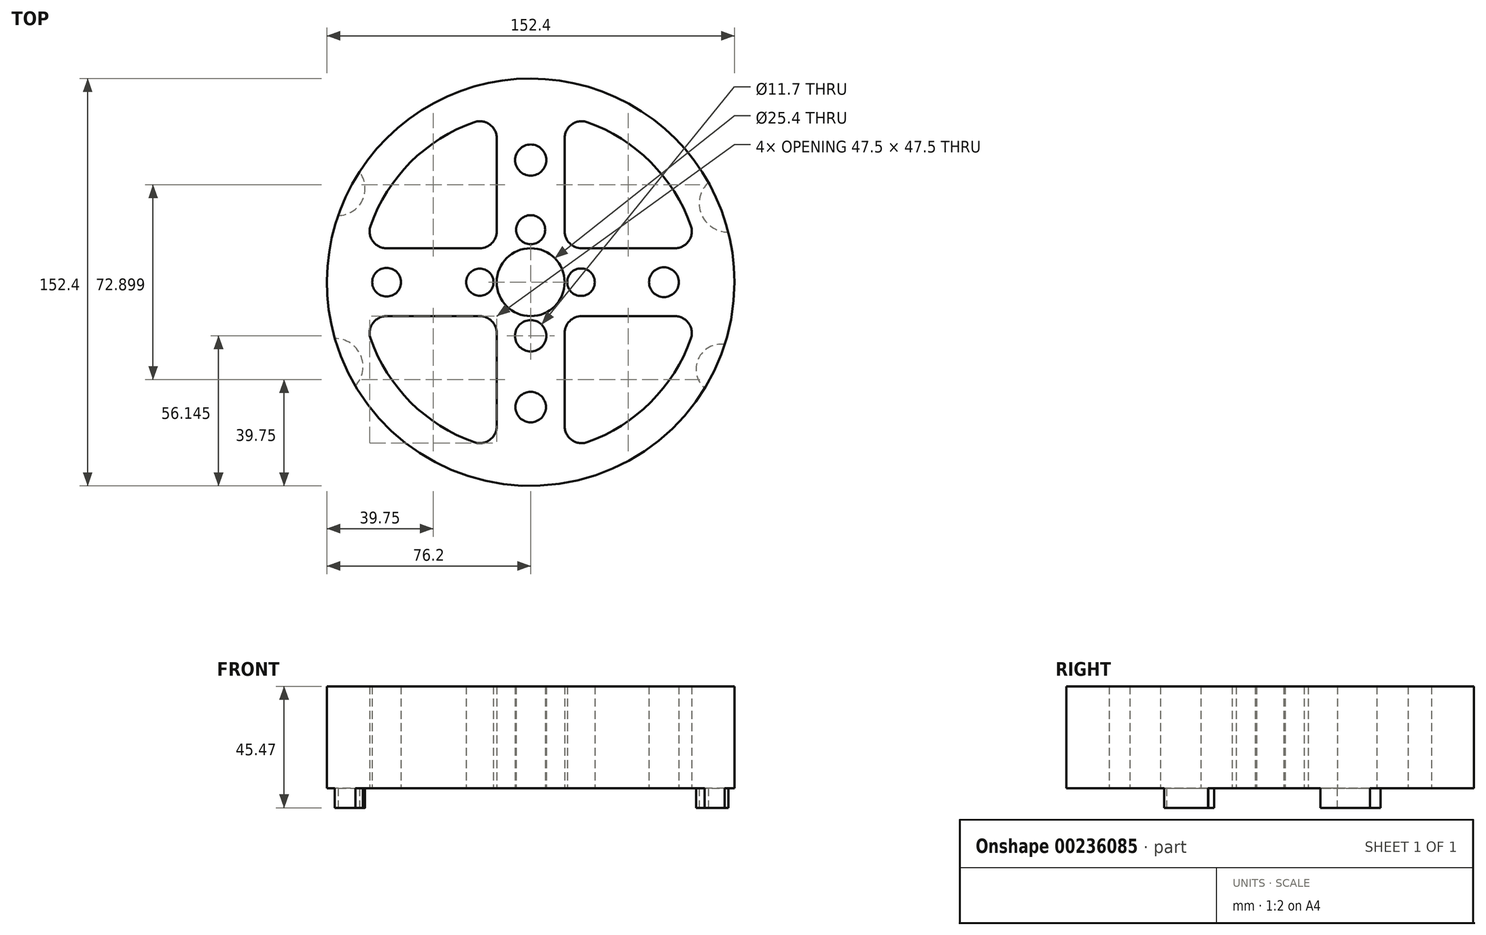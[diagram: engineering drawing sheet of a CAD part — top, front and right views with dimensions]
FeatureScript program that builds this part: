
annotation { "Feature Type Name" : "Feature", "Feature Type Description" : "" }
export const myFeature = defineFeature(function(context is Context, id is Id, definition is map)
    precondition{}
    {
        {
            var Q0;
            Q0=qCreatedBy(makeId("Top.planeOp"),FACE);
            var sketch = newSketch(context, id + "F0", { "sketchPlane" : qUnion([Q0])});
            skCircle(sketch, "E0", {"center": v(0, 0) * mm, "radius": 76.2 * mm});
            skArc(sketch, "E1", {"start": v(-21.17, 59.87) * mm, "mid": v(-44.9, 44.9) * mm, "end": v(-59.87, 21.17) * mm});
            skCircle(sketch, "E2", {"center": v(0, 0) * mm, "radius": 12.7 * mm});
            skLineSegment(sketch, "E3", {"start": v(0, 0) * mm, "end": v(0, 76.2) * mm});
            skLineSegment(sketch, "E4.0", {"start": v(12.7, 19.05) * mm, "end": v(12.7, 53.88) * mm});
            skLineSegment(sketch, "E5.0", {"start": v(-12.7, 19.05) * mm, "end": v(-12.7, 53.88) * mm});
            skLineSegment(sketch, "E6", {"start": v(0, 0) * mm, "end": v(0, -76.2) * mm});
            skLineSegment(sketch, "E7", {"start": v(0, 0) * mm, "end": v(76.2, 0) * mm});
            skLineSegment(sketch, "E8", {"start": v(0, 0) * mm, "end": v(-76.2, 0) * mm});
            skLineSegment(sketch, "E9.0", {"start": v(19.05, -12.7) * mm, "end": v(53.88, -12.7) * mm});
            skLineSegment(sketch, "E10.0", {"start": v(19.05, 12.7) * mm, "end": v(53.88, 12.7) * mm});
            skLineSegment(sketch, "E11.0", {"start": v(-12.7, -19.05) * mm, "end": v(-12.7, -53.88) * mm});
            skLineSegment(sketch, "E12.0", {"start": v(12.7, -19.05) * mm, "end": v(12.7, -53.88) * mm});
            skLineSegment(sketch, "E13.0", {"start": v(-19.05, 12.7) * mm, "end": v(-53.88, 12.7) * mm});
            skLineSegment(sketch, "E14.0", {"start": v(-19.05, -12.7) * mm, "end": v(-53.88, -12.7) * mm});
            skArc(sketch, "E15.trimOffspring", {"start": v(59.87, 21.17) * mm, "mid": v(44.9, 44.9) * mm, "end": v(21.17, 59.87) * mm});
            skLineSegment(sketch, "E16.trimOffspring", {"start": v(75.13, -12.7) * mm, "end": v(76.2, -12.7) * mm});
            skLineSegment(sketch, "E17.trimOffspring", {"start": v(75.13, 12.7) * mm, "end": v(76.2, 12.7) * mm});
            skArc(sketch, "E18.trimOffspring", {"start": v(-59.87, -21.17) * mm, "mid": v(-44.9, -44.9) * mm, "end": v(-21.17, -59.87) * mm});
            skArc(sketch, "E19.trimOffspring", {"start": v(21.17, -59.87) * mm, "mid": v(44.9, -44.9) * mm, "end": v(59.87, -21.17) * mm});
            skLineSegment(sketch, "E20.trimOffspring", {"start": v(-12.7, -75.13) * mm, "end": v(-12.7, -76.2) * mm});
            skLineSegment(sketch, "E21.trimOffspring", {"start": v(12.7, -75.13) * mm, "end": v(12.7, -76.2) * mm});
            skLineSegment(sketch, "E22.trimOffspring", {"start": v(-75.13, 12.7) * mm, "end": v(-76.2, 12.7) * mm});
            skLineSegment(sketch, "E23.trimOffspring", {"start": v(-12.7, 75.13) * mm, "end": v(-12.7, 76.2) * mm});
            skLineSegment(sketch, "E24.trimOffspring", {"start": v(12.7, 75.13) * mm, "end": v(12.7, 76.2) * mm});
            skPoint(sketch, "E25.visualSharp", {"position": v(12.7, 62.22) * mm});
            skArc(sketch, "E25.filletArc", {"start": v(21.17, 59.87) * mm, "mid": v(15.38, 59.07) * mm, "end": v(12.7, 53.88) * mm});
            skPoint(sketch, "E26.visualSharp", {"position": v(12.7, 12.7) * mm});
            skArc(sketch, "E26.filletArc", {"start": v(12.7, 19.05) * mm, "mid": v(14.56, 14.56) * mm, "end": v(19.05, 12.7) * mm});
            skPoint(sketch, "E27.visualSharp", {"position": v(62.22, 12.7) * mm});
            skArc(sketch, "E27.filletArc", {"start": v(53.88, 12.7) * mm, "mid": v(59.07, 15.38) * mm, "end": v(59.87, 21.17) * mm});
            skPoint(sketch, "E28.visualSharp", {"position": v(-12.7, 62.22) * mm});
            skArc(sketch, "E28.filletArc", {"start": v(-12.7, 53.88) * mm, "mid": v(-15.38, 59.07) * mm, "end": v(-21.17, 59.87) * mm});
            skPoint(sketch, "E29.visualSharp", {"position": v(-12.7, 12.7) * mm});
            skArc(sketch, "E29.filletArc", {"start": v(-19.05, 12.7) * mm, "mid": v(-14.56, 14.56) * mm, "end": v(-12.7, 19.05) * mm});
            skPoint(sketch, "E30.visualSharp", {"position": v(-62.22, 12.7) * mm});
            skArc(sketch, "E30.filletArc", {"start": v(-59.87, 21.17) * mm, "mid": v(-59.07, 15.38) * mm, "end": v(-53.88, 12.7) * mm});
            skPoint(sketch, "E31.visualSharp", {"position": v(-12.7, -12.7) * mm});
            skArc(sketch, "E31.filletArc", {"start": v(-12.7, -19.05) * mm, "mid": v(-14.56, -14.56) * mm, "end": v(-19.05, -12.7) * mm});
            skPoint(sketch, "E32.visualSharp", {"position": v(-12.7, -62.22) * mm});
            skArc(sketch, "E32.filletArc", {"start": v(-21.17, -59.87) * mm, "mid": v(-15.38, -59.07) * mm, "end": v(-12.7, -53.88) * mm});
            skPoint(sketch, "E33.visualSharp", {"position": v(-62.22, -12.7) * mm});
            skArc(sketch, "E33.filletArc", {"start": v(-53.88, -12.7) * mm, "mid": v(-59.07, -15.38) * mm, "end": v(-59.87, -21.17) * mm});
            skPoint(sketch, "E34.visualSharp", {"position": v(12.7, -12.7) * mm});
            skArc(sketch, "E34.filletArc", {"start": v(19.05, -12.7) * mm, "mid": v(14.56, -14.56) * mm, "end": v(12.7, -19.05) * mm});
            skPoint(sketch, "E35.visualSharp", {"position": v(12.7, -62.22) * mm});
            skArc(sketch, "E35.filletArc", {"start": v(12.7, -53.88) * mm, "mid": v(15.38, -59.07) * mm, "end": v(21.17, -59.87) * mm});
            skPoint(sketch, "E36.visualSharp", {"position": v(62.22, -12.7) * mm});
            skArc(sketch, "E36.filletArc", {"start": v(59.87, -21.17) * mm, "mid": v(59.07, -15.38) * mm, "end": v(53.88, -12.7) * mm});
            skArc(sketch, "E37", {"start": v(-72, 24.96) * mm, "mid": v(-62.94, 30.64) * mm, "end": v(-64.06, 41.27) * mm});
            skArc(sketch, "E38", {"start": v(-65.57, -38.83) * mm, "mid": v(-63.56, -27.41) * mm, "end": v(-73.24, -21.04) * mm});
            skArc(sketch, "E39", {"start": v(72.55, -23.3) * mm, "mid": v(62.67, -28.7) * mm, "end": v(65.03, -39.72) * mm});
            skArc(sketch, "E40", {"start": v(66.43, 37.33) * mm, "mid": v(63.8, 25.5) * mm, "end": v(73.86, 18.73) * mm});
            skLineSegment(sketch, "E41", {"start": v(-53.88, 0) * mm, "end": v(-19.02, 0) * mm});
            skCircle(sketch, "E42", {"center": v(-53.88, 0) * mm, "radius": 5.38 * mm});
            skCircle(sketch, "E43", {"center": v(-19.02, 0) * mm, "radius": 5.1 * mm});
            skCircle(sketch, "E44", {"center": v(18.81, 0) * mm, "radius": 5.14 * mm});
            skCircle(sketch, "E45", {"center": v(49.83, 0) * mm, "radius": 5.56 * mm});
            skCircle(sketch, "E46", {"center": v(0, -20.06) * mm, "radius": 5.85 * mm});
            skCircle(sketch, "E47", {"center": v(0, -46.73) * mm, "radius": 5.7 * mm});
            skCircle(sketch, "E48", {"center": v(0, 19.64) * mm, "radius": 5.43 * mm});
            skCircle(sketch, "E49", {"center": v(0, 45.7) * mm, "radius": 5.83 * mm});
            skSolve(sketch);
        }
        {
            var Q0;
            Q0 = qSketchRegion(id + "F0", true);
            extrude(context, id + "F1", {"entities" : qUnion([Q0]), "endBound" : BoundingType.SYMMETRIC, "depth" : 25.4 * mm});
        }
        {
            var Q0;
            {var subQ0=sQuery(id+"F0.wireOp",EDGE,"E37");Q0=makeQuery(id+"F0.imprint","IMPRINT",FACE,{"disambiguationData":[TD([[makeQuery(id+"F0.imprint","IMPRINT",EDGE,{"derivedFrom":subQ0}),1.0]])]});}
            var Q1;
            {var subQ0=sQuery(id+"F0.wireOp",EDGE,"E38");Q1=makeQuery(id+"F0.imprint","IMPRINT",FACE,{"disambiguationData":[TD([[makeQuery(id+"F0.imprint","IMPRINT",EDGE,{"derivedFrom":subQ0}),1.0]])]});}
            var Q2;
            {var subQ0=sQuery(id+"F0.wireOp",EDGE,"E39");Q2=makeQuery(id+"F0.imprint","IMPRINT",FACE,{"disambiguationData":[TD([[makeQuery(id+"F0.imprint","IMPRINT",EDGE,{"derivedFrom":subQ0}),1.0]])]});}
            var Q3;
            {var subQ0=sQuery(id+"F0.wireOp",EDGE,"E40");Q3=makeQuery(id+"F0.imprint","IMPRINT",FACE,{"disambiguationData":[TD([[makeQuery(id+"F0.imprint","IMPRINT",EDGE,{"derivedFrom":subQ0}),1.0]])]});}
            extrude(context, id + "F2", {"entities" : qUnion([Q0, Q1, Q2, Q3]), "operationType" : NewBodyOperationType.ADD, "endBound" : BoundingType.SYMMETRIC, "depth" : 40.13 * mm});
        }
        {
            var Q0;
            Q0 = qSketchRegion(id + "F0", true);
            extrude(context, id + "F3", {"entities" : qUnion([Q0]), "operationType" : NewBodyOperationType.ADD, "depth" : 25.4 * mm});
        }
    });
